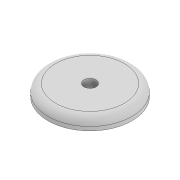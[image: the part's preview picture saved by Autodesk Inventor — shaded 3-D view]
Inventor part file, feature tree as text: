
AUTODESK INVENTOR PART (.ipt)
format: ipt  version: 2022 (Build 260153000, 153)  size: 106,496 bytes
history: native  units: mm
features: extrude x1, fillet x1, sketch x1
ambient origin geometry x8: Origin, YZ Plane, XZ Plane, XY Plane, X Axis, Y Axis, Z Axis, Center Point
bodies: Solid1 (feature_tree)
feature tree (3):
  extrude  "Extrusion1"  Depth=2.0mm
  fillet  "Fillet1"  Radius=3.0mm
  sketch  "Sketch1"  dims[d0=22.0mm d1=3.2mm d2=3.0mm d3=0.0mm d4=2.0mm]
